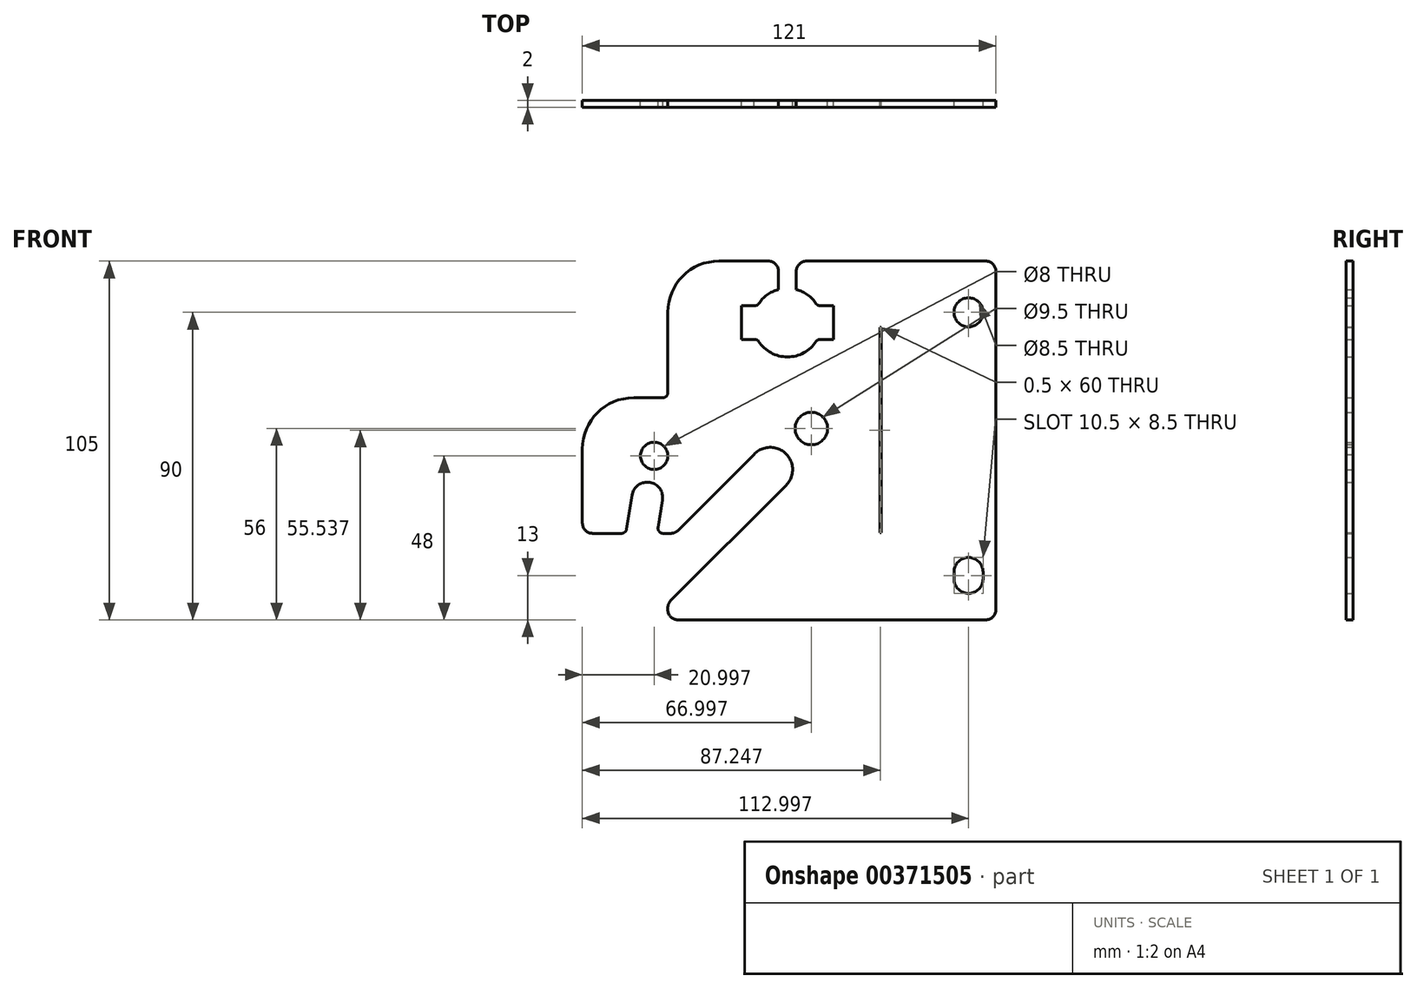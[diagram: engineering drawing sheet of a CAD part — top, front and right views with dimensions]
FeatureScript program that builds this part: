
annotation { "Feature Type Name" : "Feature", "Feature Type Description" : "" }
export const myFeature = defineFeature(function(context is Context, id is Id, definition is map)
    precondition{}
    {
        {
            var Q0;
            Q0=qCreatedBy(makeId("Front.planeOp"),FACE);
            var sketch = newSketch(context, id + "F0", { "sketchPlane" : qUnion([Q0])});
            skLineSegment(sketch, "E0.bottom", {"start": v(159.7, 0) * mm, "end": v(255.7, 0) * mm});
            skLineSegment(sketch, "E0.top", {"start": v(159.7, 105) * mm, "end": v(192.1, 105) * mm});
            skLineSegment(sketch, "E0.left", {"start": v(159.7, 0) * mm, "end": v(159.7, 4.8) * mm});
            skLineSegment(sketch, "E0.right", {"start": v(255.7, 0) * mm, "end": v(255.7, 105) * mm});
            skLineSegment(sketch, "E1", {"start": v(159.7, 65) * mm, "end": v(134.7, 65) * mm});
            skLineSegment(sketch, "E2", {"start": v(134.7, 65) * mm, "end": v(134.7, 25.32) * mm});
            skLineSegment(sketch, "E3", {"start": v(134.7, 25.32) * mm, "end": v(147.41, 25.32) * mm});
            skLineSegment(sketch, "E4.trimOffspring", {"start": v(159.7, 65) * mm, "end": v(159.7, 105) * mm});
            skCircle(sketch, "E5", {"center": v(247.7, 90) * mm, "radius": 4.25 * mm});
            skLineSegment(sketch, "E6", {"start": v(221.7, 115) * mm, "end": v(221.7, -22.06) * mm, "construction": true});
            skLineSegment(sketch, "E7", {"start": v(-142.35, 0) * mm, "end": v(321.86, 0) * mm, "construction": true});
            skCircle(sketch, "E8", {"center": v(201.7, 56) * mm, "radius": 4.75 * mm});
            skArc(sketch, "E9", {"start": v(194.3, 39.4) * mm, "mid": v(194.2, 48.7) * mm, "end": v(184.9, 48.4) * mm});
            skLineSegment(sketch, "E10", {"start": v(189.7, 44) * mm, "end": v(157.45, 11.75) * mm, "construction": true});
            skLineSegment(sketch, "E11", {"start": v(184.9, 48.4) * mm, "end": v(163.06, 26.56) * mm});
            skLineSegment(sketch, "E12", {"start": v(194.3, 39.4) * mm, "end": v(159.7, 4.8) * mm});
            skCircle(sketch, "E13", {"center": v(155.7, 48) * mm, "radius": 4 * mm});
            skLineSegment(sketch, "E14", {"start": v(155.7, 48) * mm, "end": v(150.16, 14.25) * mm, "construction": true});
            skArc(sketch, "E15", {"start": v(158.14, 35.09) * mm, "mid": v(154.43, 40.26) * mm, "end": v(149.26, 36.54) * mm});
            skLineSegment(sketch, "E16", {"start": v(158.14, 35.09) * mm, "end": v(156.53, 25.32) * mm});
            skLineSegment(sketch, "E17", {"start": v(149.26, 36.54) * mm, "end": v(147.41, 25.32) * mm});
            skLineSegment(sketch, "E18", {"start": v(169.75, 87) * mm, "end": v(216.87, 87) * mm, "construction": true});
            skLineSegment(sketch, "E19", {"start": v(194.7, 109.48) * mm, "end": v(194.7, 75.12) * mm, "construction": true});
            skArc(sketch, "E20", {"start": v(203.41, 92) * mm, "mid": v(200.83, 94.96) * mm, "end": v(197.3, 96.7) * mm});
            skLineSegment(sketch, "E21.bottom", {"start": v(181.2, 92) * mm, "end": v(185.98, 92) * mm});
            skLineSegment(sketch, "E21.top", {"start": v(181.2, 82) * mm, "end": v(185.98, 82) * mm});
            skLineSegment(sketch, "E21.left", {"start": v(181.2, 92) * mm, "end": v(181.2, 82) * mm});
            skLineSegment(sketch, "E21.right", {"start": v(208.2, 92) * mm, "end": v(208.2, 82) * mm});
            skLineSegment(sketch, "E22.trimOffspring", {"start": v(203.41, 92) * mm, "end": v(208.2, 92) * mm});
            skArc(sketch, "E23.trimOffspring", {"start": v(185.98, 82) * mm, "mid": v(194.7, 76.95) * mm, "end": v(203.41, 82) * mm});
            skLineSegment(sketch, "E24.trimOffspring", {"start": v(203.41, 82) * mm, "end": v(208.2, 82) * mm});
            skLineSegment(sketch, "E25", {"start": v(0, 0) * mm, "end": v(0, 99.82) * mm, "construction": true});
            skLineSegment(sketch, "E26", {"start": v(247.7, 90) * mm, "end": v(247.7, 2.04) * mm, "construction": true});
            skArc(sketch, "E27", {"start": v(243.45, 12) * mm, "mid": v(247.7, 7.75) * mm, "end": v(251.95, 12) * mm});
            skLineSegment(sketch, "E28", {"start": v(221.7, 85.54) * mm, "end": v(221.7, 25.54) * mm});
            skLineSegment(sketch, "E29", {"start": v(221.7, 25.54) * mm, "end": v(222.2, 25.54) * mm});
            skLineSegment(sketch, "E30", {"start": v(222.2, 25.54) * mm, "end": v(222.2, 85.54) * mm});
            skLineSegment(sketch, "E31", {"start": v(222.2, 85.54) * mm, "end": v(221.7, 85.54) * mm});
            skLineSegment(sketch, "E32", {"start": v(192.1, 105) * mm, "end": v(192.1, 96.7) * mm});
            skLineSegment(sketch, "E33.MirrorCS", {"start": v(197.3, 105) * mm, "end": v(197.3, 96.7) * mm});
            skLineSegment(sketch, "E34.trimOffspring", {"start": v(197.3, 105) * mm, "end": v(255.7, 105) * mm});
            skArc(sketch, "E35.trimOffspring", {"start": v(192.1, 96.7) * mm, "mid": v(188.57, 94.96) * mm, "end": v(185.98, 92) * mm});
            skArc(sketch, "E36", {"start": v(251.95, 14) * mm, "mid": v(247.7, 18.25) * mm, "end": v(243.45, 14) * mm});
            skLineSegment(sketch, "E37", {"start": v(251.95, 14) * mm, "end": v(251.95, 12) * mm});
            skLineSegment(sketch, "E38", {"start": v(243.45, 14) * mm, "end": v(243.45, 12) * mm});
            skLineSegment(sketch, "E39", {"start": v(156.53, 25.32) * mm, "end": v(161.82, 25.32) * mm});
            skLineSegment(sketch, "E40", {"start": v(163.06, 26.56) * mm, "end": v(161.82, 25.32) * mm});
            skSolve(sketch);
        }
        {
            var Q0;
            Q0=makeQuery(id+"F0.imprint","IMPRINT",FACE,{"disambiguationData":[TD([[makeQuery(id+"F0.imprint","IMPRINT",EDGE,{"derivedFrom":sQuery(id+"F0.wireOp",EDGE,"RRyUBbn2-GDR9-CAo5-2geO-ZO30nfhzrQTg")}),1.0]])]});
            var Q1;
            Q1=makeQuery(id+"F0.imprint","IMPRINT",FACE,{"disambiguationData":[TD([[makeQuery(id+"F0.imprint","IMPRINT",EDGE,{"derivedFrom":sQuery(id+"F0.wireOp",EDGE,"E0.bottom")}),1.0]])]});
            extrude(context, id + "F1", {"entities" : qUnion([Q0, Q1]), "depth" : 2 * mm, "offsetDistance" : 25 * mm});
        }
        {
            var Q0;
            Q0=makeQuery(id+"F1.opExtrude","SWEPT_EDGE",EDGE,{"disambiguationData":[OSD([sQuery(id+"F0.wireOp",EDGE,"E1"),sQuery(id+"F0.wireOp",EDGE,"E2")])]});
            var Q1;
            Q1=makeQuery(id+"F1.opExtrude","SWEPT_EDGE",EDGE,{"disambiguationData":[OSD([sQuery(id+"F0.wireOp",EDGE,"E0.top"),sQuery(id+"F0.wireOp",EDGE,"E4.trimOffspring")])]});
            fillet(context, id + "F2", {"entities" : qUnion([Q0, Q1]), "tangentPropagation" : true, "radius" : 15 * mm, "defaultsChanged" : false, "vertexSettings" : [], "allowEdgeOverflow" : false});
        }
        {
            var Q0;
            Q0=makeQuery(id+"F1.opExtrude","SWEPT_EDGE",EDGE,{"disambiguationData":[OSD([sQuery(id+"F0.wireOp",EDGE,"E0.right"),sQuery(id+"F0.wireOp",EDGE,"E34.trimOffspring")])]});
            var Q1;
            Q1=makeQuery(id+"F1.opExtrude","SWEPT_EDGE",EDGE,{"disambiguationData":[OSD([sQuery(id+"F0.wireOp",EDGE,"E0.bottom"),sQuery(id+"F0.wireOp",EDGE,"E0.right")])]});
            var Q2;
            Q2=makeQuery(id+"F1.opExtrude","SWEPT_EDGE",EDGE,{"disambiguationData":[OSD([sQuery(id+"F0.wireOp",EDGE,"E33.MirrorCS"),sQuery(id+"F0.wireOp",EDGE,"E34.trimOffspring")])]});
            var Q3;
            Q3=makeQuery(id+"F1.opExtrude","SWEPT_EDGE",EDGE,{"disambiguationData":[OSD([sQuery(id+"F0.wireOp",EDGE,"E0.top"),sQuery(id+"F0.wireOp",EDGE,"E32")])]});
            var Q4;
            Q4=makeQuery(id+"F1.opExtrude","SWEPT_EDGE",EDGE,{"disambiguationData":[OSD([sQuery(id+"F0.wireOp",EDGE,"E39"),sQuery(id+"F0.wireOp",EDGE,"E40")])]});
            var Q5;
            Q5=makeQuery(id+"F1.opExtrude","SWEPT_EDGE",EDGE,{"disambiguationData":[OSD([sQuery(id+"F0.wireOp",EDGE,"E0.left"),sQuery(id+"F0.wireOp",EDGE,"E12")])]});
            var Q6;
            Q6=makeQuery(id+"F1.opExtrude","SWEPT_EDGE",EDGE,{"disambiguationData":[OSD([sQuery(id+"F0.wireOp",EDGE,"E0.bottom"),sQuery(id+"F0.wireOp",EDGE,"E0.left")])]});
            var Q7;
            Q7=makeQuery(id+"F1.opExtrude","SWEPT_EDGE",EDGE,{"disambiguationData":[OSD([sQuery(id+"F0.wireOp",EDGE,"E2"),sQuery(id+"F0.wireOp",EDGE,"E3")])]});
            fillet(context, id + "F3", {"entities" : qUnion([Q0, Q1, Q2, Q3, Q4, Q5, Q6, Q7]), "tangentPropagation" : true, "radius" : 3 * mm, "defaultsChanged" : false, "vertexSettings" : [], "allowEdgeOverflow" : false});
        }
        {
            var Q0;
            Q0=makeQuery(id+"F1.opExtrude","SWEPT_EDGE",EDGE,{"disambiguationData":[OSD([sQuery(id+"F0.wireOp",EDGE,"E3"),sQuery(id+"F0.wireOp",EDGE,"E17")])]});
            var Q1;
            Q1=makeQuery(id+"F1.opExtrude","SWEPT_EDGE",EDGE,{"disambiguationData":[OSD([sQuery(id+"F0.wireOp",EDGE,"E16"),sQuery(id+"F0.wireOp",EDGE,"E39")])]});
            var Q2;
            Q2=makeQuery(id+"F1.opExtrude","SWEPT_EDGE",EDGE,{"disambiguationData":[OSD([sQuery(id+"F0.wireOp",EDGE,"E1"),sQuery(id+"F0.wireOp",EDGE,"E4.trimOffspring")])]});
            fillet(context, id + "F4", {"entities" : qUnion([Q0, Q1, Q2]), "tangentPropagation" : true, "radius" : 1.5 * mm, "defaultsChanged" : false, "vertexSettings" : [], "allowEdgeOverflow" : false});
        }
        {
            var Q0;
            Q0=makeQuery(id+"F1.opExtrude","SWEPT_EDGE",EDGE,{"disambiguationData":[OSD([sQuery(id+"F0.wireOp",EDGE,"E21.bottom"),sQuery(id+"F0.wireOp",EDGE,"E35.trimOffspring")])]});
            var Q1;
            Q1=makeQuery(id+"F1.opExtrude","SWEPT_EDGE",EDGE,{"disambiguationData":[OSD([sQuery(id+"F0.wireOp",EDGE,"E21.top"),sQuery(id+"F0.wireOp",EDGE,"E23.trimOffspring")])]});
            var Q2;
            Q2=makeQuery(id+"F1.opExtrude","SWEPT_EDGE",EDGE,{"disambiguationData":[OSD([sQuery(id+"F0.wireOp",EDGE,"E20"),sQuery(id+"F0.wireOp",EDGE,"E22.trimOffspring")])]});
            var Q3;
            Q3=makeQuery(id+"F1.opExtrude","SWEPT_EDGE",EDGE,{"disambiguationData":[OSD([sQuery(id+"F0.wireOp",EDGE,"E23.trimOffspring"),sQuery(id+"F0.wireOp",EDGE,"E24.trimOffspring")])]});
            fillet(context, id + "F5", {"entities" : qUnion([Q0, Q1, Q2, Q3]), "tangentPropagation" : true, "radius" : 1 * mm, "defaultsChanged" : false, "vertexSettings" : [], "allowEdgeOverflow" : false});
        }
    });
